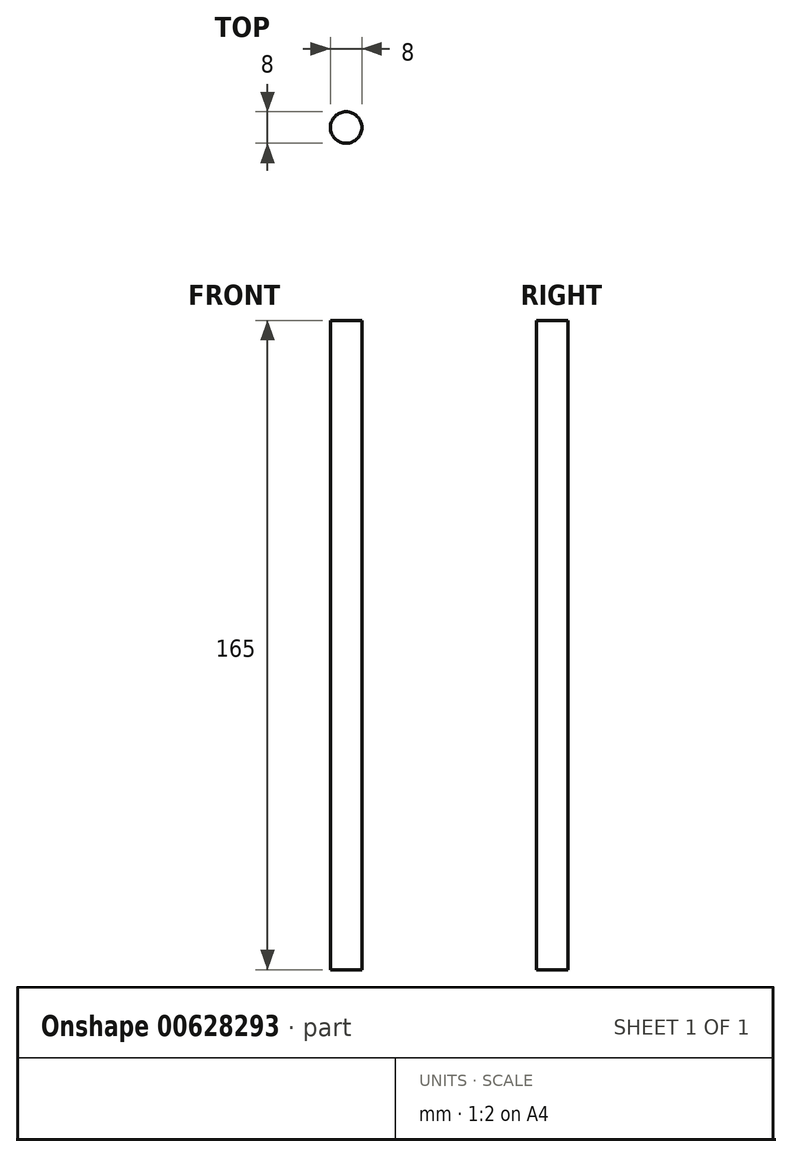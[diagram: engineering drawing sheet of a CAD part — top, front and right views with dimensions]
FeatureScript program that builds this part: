
annotation { "Feature Type Name" : "Feature", "Feature Type Description" : "" }
export const myFeature = defineFeature(function(context is Context, id is Id, definition is map)
    precondition{}
    {
        {
            var Q0;
            Q0=qCreatedBy(makeId("Top.planeOp"),FACE);
            var sketch = newSketch(context, id + "F0", { "sketchPlane" : qUnion([Q0])});
            skCircle(sketch, "E0", {"center": v(0, 0) * mm, "radius": 4 * mm});
            skSolve(sketch);
        }
        {
            var Q0;
            Q0 = qSketchRegion(id + "F0", true);
            extrude(context, id + "F1", {"entities" : qUnion([Q0]), "depth" : 165 * mm, "offsetDistance" : 25 * mm});
        }
    });
